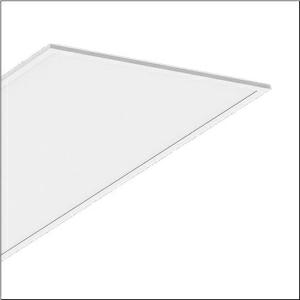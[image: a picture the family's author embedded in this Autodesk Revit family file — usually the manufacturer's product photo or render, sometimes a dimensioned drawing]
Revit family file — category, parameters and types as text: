
# Revit family: apollon_21_linear_51mq1awd2m14
name_source: partatom
category: Lighting Fixtures
units: mm (PartAtom-declared; Revit-internal decimal feet)

## family parameters
Cut with Voids When Loaded = No
Host = Face
Light Source = No
Part Type = Normal
Room Calculation Point = No
Round Connector Dimension = Use Diameter
Shared = No

## types (1)
- --- (1 x LED, 7000 lm, 44.5 W, 4000K)
    Apparent Load = 45 VA
    CIE Flux Codes = 60 87 97 100 100
    Color Rendering = 80
    Color Temperature = 4000K
    Default Elevation = 1800 mm
    Description = Apollon 21 linear, office luminaire, primary optical cover: micro prismatic cover, of PMMA, CAT 2 (L<= 3000cd/m²), light emission: direct distribution, primary light characteristic: symmetric, installation type: lay-in mounting, recessed, LED, rated luminous flux: 7.820lm, luminous efficacy: 173lm/W, light colour: 830/840, colour temperature: 3000/4000K, control gear: DALI 2, Multilumen, with terminal, 5-pole, mains connection: 220..240V, AC/DC, 0/50..60Hz, rated input power: 45.3W, suitable for self-contained emergency lighting element 59MQE002602A with integrated self-test function according to EN 60598-2-22, housing, of aluminium, coated, traffic white (RAL 9016), module: M600, length: 1.195mm, width: 595mm, height: 55mm, housing upper side, of sheet steel, galvanised, protection rating (complete): IP20, protection rating (lamp compartment, on room side): IP50, insulation class (complete): insulation class II (safety insulation), certification: CE, ENEC, UKCA, impact resistance: IK03, permissible operating ambient temperature: -20..+45°C, standard: EN 60598-2-22, corresponds to IFS (International Featured Standards) requirements for safety and quality in the food industry, packaging unit: 1 piece
    Height = 0 mm  [stored 0 ft]
    Lamp = 1 x LED
    Lamp Light Flux = 7000 lm
    Lamp Power = 44.5 W
    Lamp count = 1
    Length = 1195 mm
    Luminous efficacy = 157 lm/W
    Manufacturer = Siteco
    ModVariant = No
    Model = 51MQ1AWD2M14
    Mounting Place = Ceiling
    Mounting Type = Recessed
    Number of Poles = 1
    OnlyDefault = Yes
    Power Factor = 1
    Product Name = Apollon 21 linear
    Product group = office luminaire | ceiling recessed
    ProductGroupID = 400
    Protection Class = Protection class II
    Protection Degree = IP 20
    RLX_Detail_Level = 1
    RLX_Emergency_Light_Flux = 0 lm
    RLX_Emergency_Type = 0
    RLX_Emergency_Type_DB = No
    RlxData = <blob elided: 22829 chars, md5=0c142f9b>
    Socket = socket
    Standby Power = 0 W
    System Light Flux = 7000 lm
    System Power = 45 W
    Type Comments = factory setting
    Type Image = l_1335551.jpg
    URL = http://relux.com
    VarID = @adj_076527
    Voltage = 0 V
    Weight = 0.00 kg
    Width = 595 mm

note: [stored X ft] marks values corroborated as IEEE doubles in the binary element streams (Revit-internal decimal feet)

## geometry (parser evidence)
native form markers: Blend x4, Sweep x9
no freeform markers — native parametric forms only
